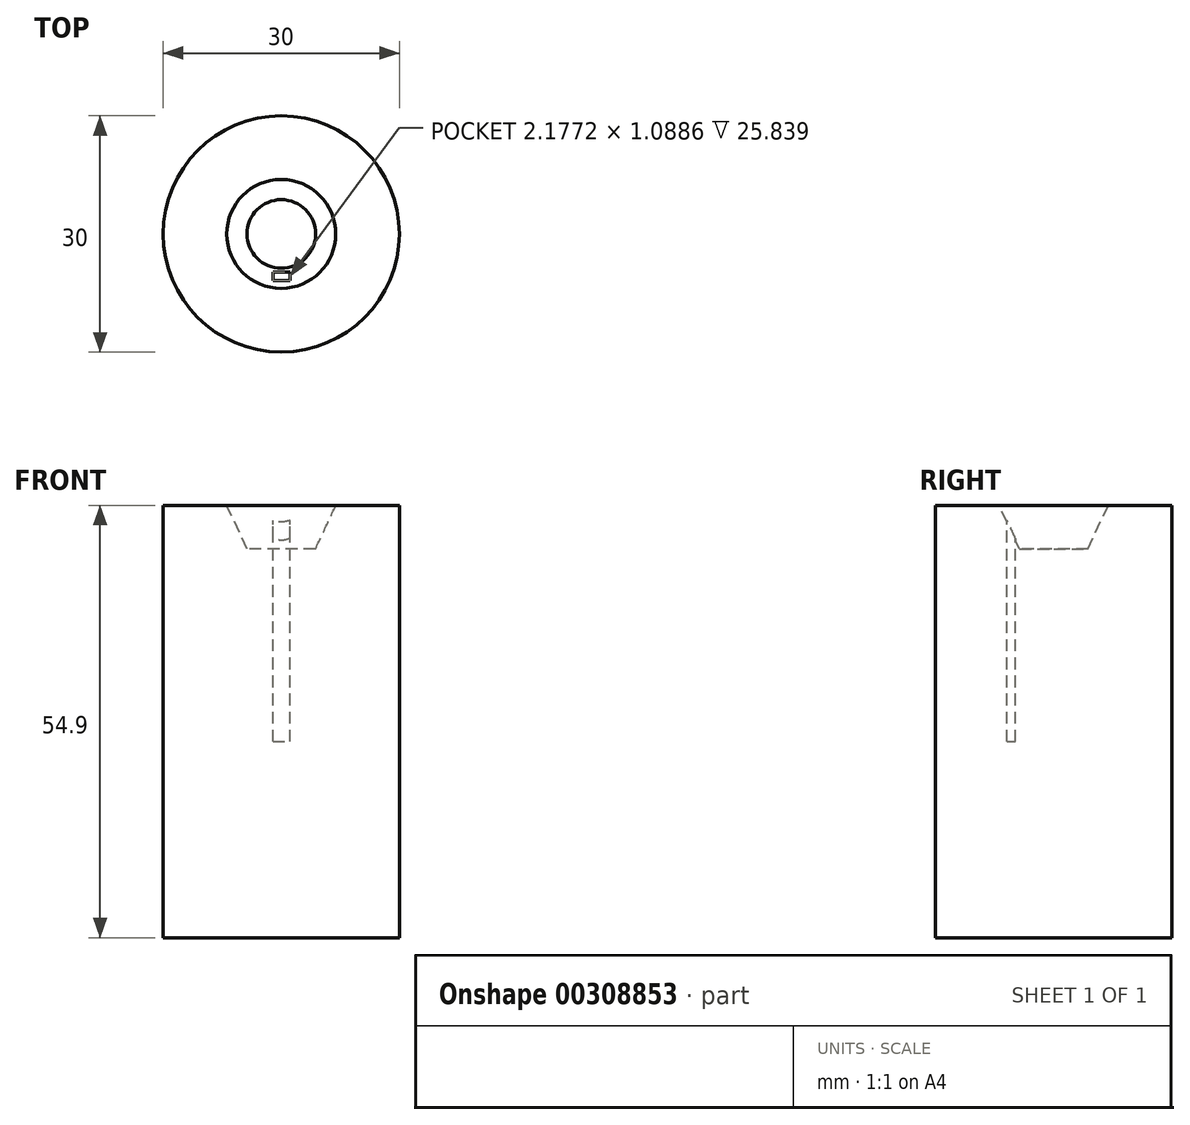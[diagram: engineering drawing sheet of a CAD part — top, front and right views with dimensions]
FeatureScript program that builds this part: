
annotation { "Feature Type Name" : "Feature", "Feature Type Description" : "" }
export const myFeature = defineFeature(function(context is Context, id is Id, definition is map)
    precondition{}
    {
        {
            var Q0;
            Q0=qCreatedBy(makeId("Top.planeOp"),FACE);
            var sketch = newSketch(context, id + "F0", { "sketchPlane" : qUnion([Q0])});
            skCircle(sketch, "E0", {"center": v(0, 0) * mm, "radius": 15 * mm});
            skSolve(sketch);
        }
        {
            var Q0;
            Q0 = qSketchRegion(id + "F0", true);
            extrude(context, id + "F1", {"entities" : qUnion([Q0]), "depth" : 54.9 * mm});
        }
        {
            var Q0;
            Q0=makeQuery(id+"F1.opExtrude","CAP_FACE",FACE,{"disambiguationData":[OSD([sQuery(id+"F0.wireOp",EDGE,"E0")])],"isStart":false});
            var sketch = newSketch(context, id + "F2", { "sketchPlane" : qUnion([Q0])});
            skCircle(sketch, "E1", {"center": v(0, 0) * mm, "radius": 6.92 * mm});
            skSolve(sketch);
        }
        {
            var Q0;
            Q0 = qSketchRegion(id + "F2", true);
            extrude(context, id + "F3", {"entities" : qUnion([Q0]), "operationType" : NewBodyOperationType.REMOVE, "oppositeDirection" : true, "depth" : 5.5 * mm, "hasDraft" : true, "draftAngle" : 25 * degree, "draftPullDirection" : true});
        }
        {
            var Q0;
            Q0=makeQuery(id+"F1.opExtrude","CAP_FACE",FACE,{"disambiguationData":[OSD([sQuery(id+"F0.wireOp",EDGE,"E0")])],"isStart":false});
            cPlane(context, id + "F4", {"entities" : qUnion([Q0]), "cplaneType" : CPlaneType.OFFSET, "offset" : 5 * mm, "oppositeDirection" : true, "width" : 150 * mm, "height" : 150 * mm});
        }
        {
            var Q0;
            Q0=qCreatedBy(id+"F4.planeOp",FACE);
            var sketch = newSketch(context, id + "F5", { "sketchPlane" : qUnion([Q0])});
            skLineSegment(sketch, "E2.bottom", {"start": v(-1.06, -5.94) * mm, "end": v(1.12, -5.94) * mm});
            skLineSegment(sketch, "E2.top", {"start": v(-1.06, -4.85) * mm, "end": v(1.12, -4.85) * mm});
            skLineSegment(sketch, "E2.left", {"start": v(-1.06, -5.94) * mm, "end": v(-1.06, -4.85) * mm});
            skLineSegment(sketch, "E2.right", {"start": v(1.12, -5.94) * mm, "end": v(1.12, -4.85) * mm});
            skSolve(sketch);
        }
        {
            var Q0;
            Q0 = qSketchRegion(id + "F5", true);
            extrude(context, id + "F6", {"entities" : qUnion([Q0]), "operationType" : NewBodyOperationType.REMOVE, "oppositeDirection" : true, "depth" : 25 * mm, "hasSecondDirection" : true, "secondDirectionOppositeDirection" : false, "secondDirectionDepth" : 25 * mm});
        }
    });
